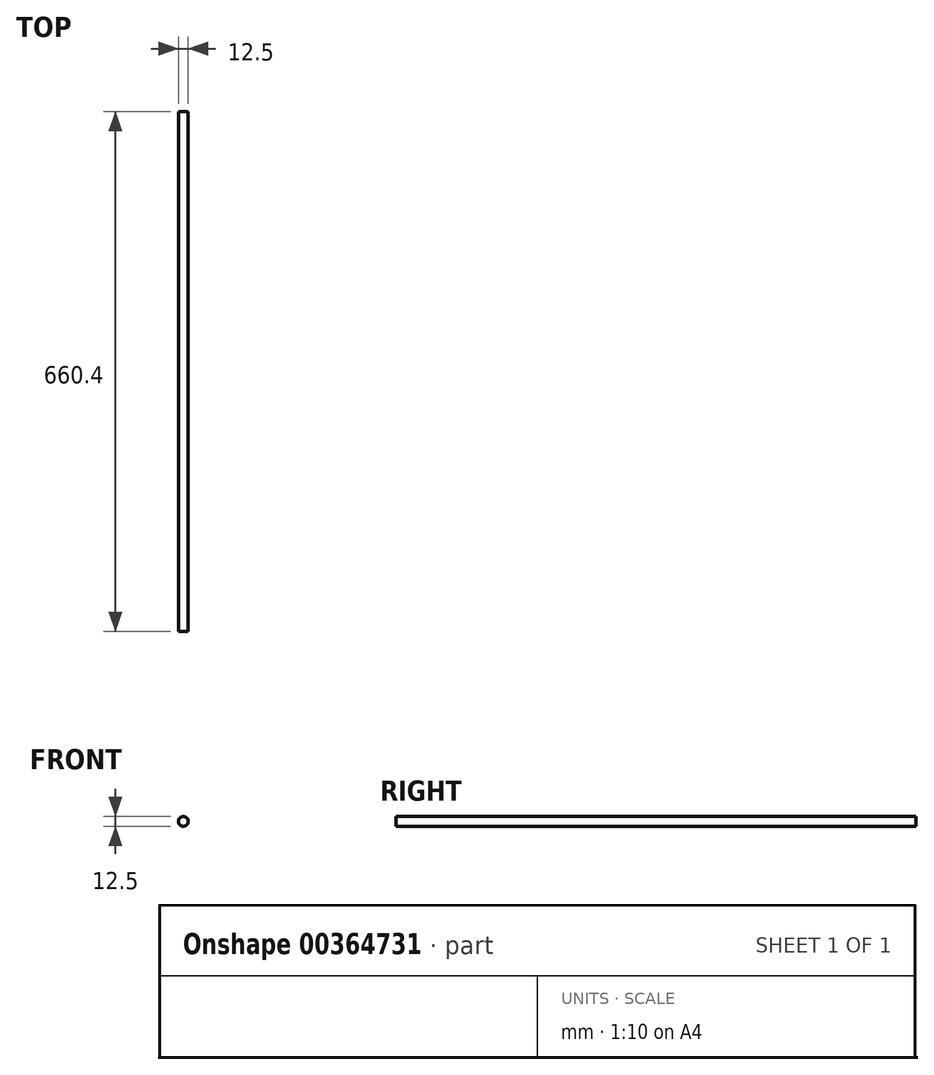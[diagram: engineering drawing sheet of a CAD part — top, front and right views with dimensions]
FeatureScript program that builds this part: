
annotation { "Feature Type Name" : "Feature", "Feature Type Description" : "" }
export const myFeature = defineFeature(function(context is Context, id is Id, definition is map)
    precondition{}
    {
        {
            var Q0;
            Q0=qCreatedBy(makeId("Front.planeOp"),FACE);
            var sketch = newSketch(context, id + "F0", { "sketchPlane" : qUnion([Q0])});
            skCircle(sketch, "E0", {"center": v(0, 0) * mm, "radius": 6.25 * mm});
            skSolve(sketch);
        }
        {
            var Q0;
            Q0 = qSketchRegion(id + "F0", true);
            extrude(context, id + "F1", {"entities" : qUnion([Q0]), "depth" : 660.4 * mm, "offsetDistance" : 25.4 * mm});
        }
    });
